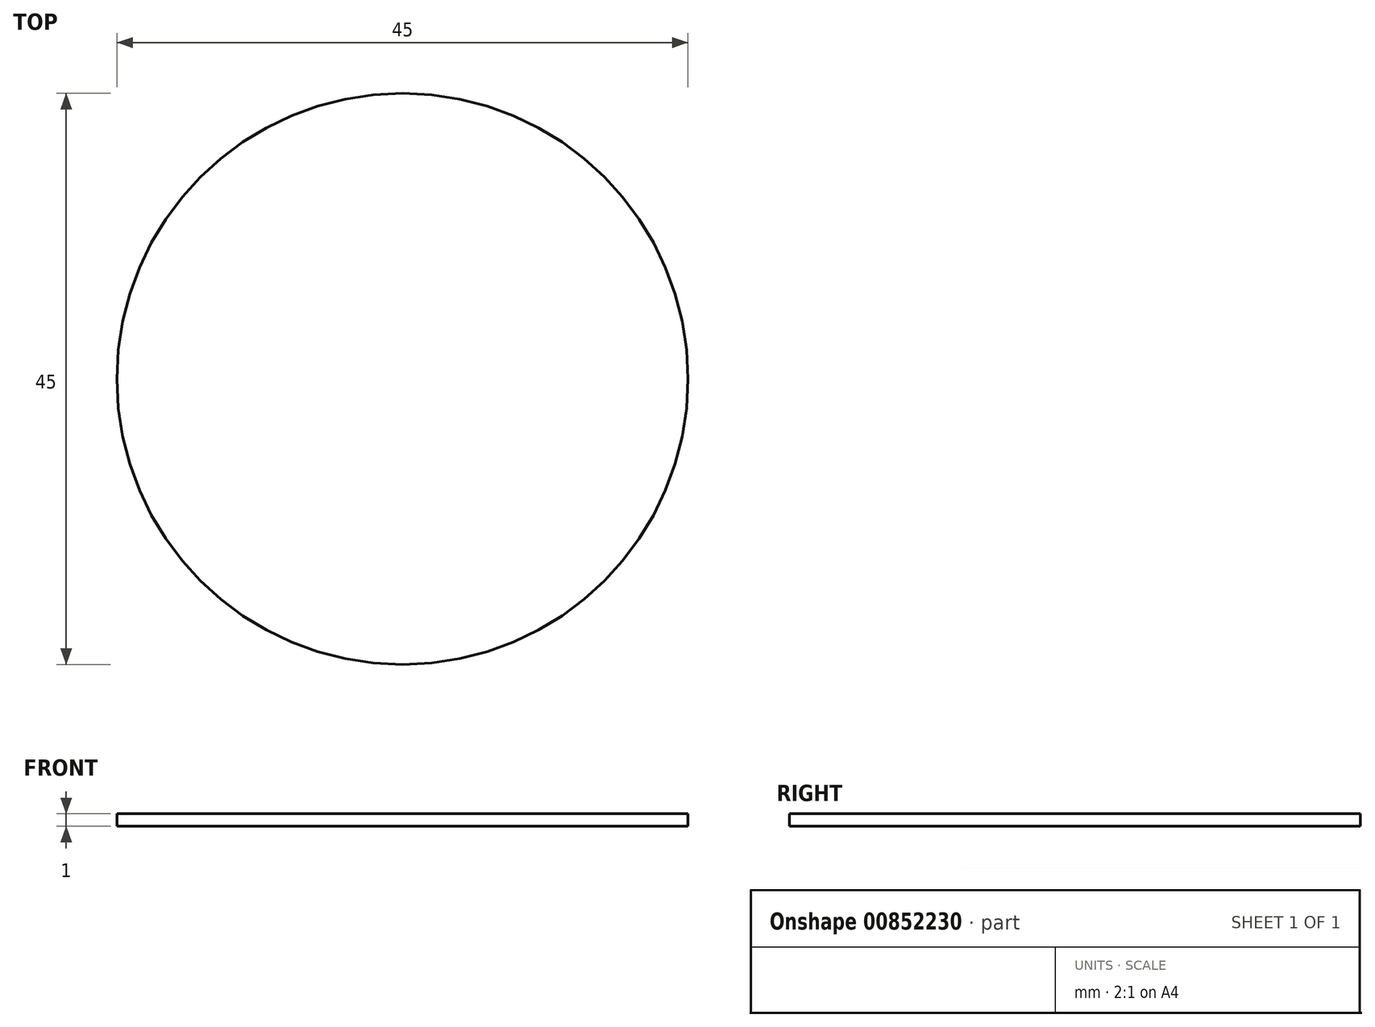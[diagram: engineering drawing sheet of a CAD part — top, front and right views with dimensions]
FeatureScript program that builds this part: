
annotation { "Feature Type Name" : "Feature", "Feature Type Description" : "" }
export const myFeature = defineFeature(function(context is Context, id is Id, definition is map)
    precondition{}
    {
        {
            var Q0;
            Q0=qCreatedBy(makeId("Top.planeOp"),FACE);
            var sketch = newSketch(context, id + "F0", { "sketchPlane" : qUnion([Q0])});
            skCircle(sketch, "E0", {"center": v(0, 0) * mm, "radius": 22.5 * mm});
            skSolve(sketch);
        }
        {
            var Q0;
            Q0 = qSketchRegion(id + "F0", true);
            extrude(context, id + "F1", {"entities" : qUnion([Q0]), "depth" : 1 * mm, "offsetDistance" : 25 * mm});
        }
    });
